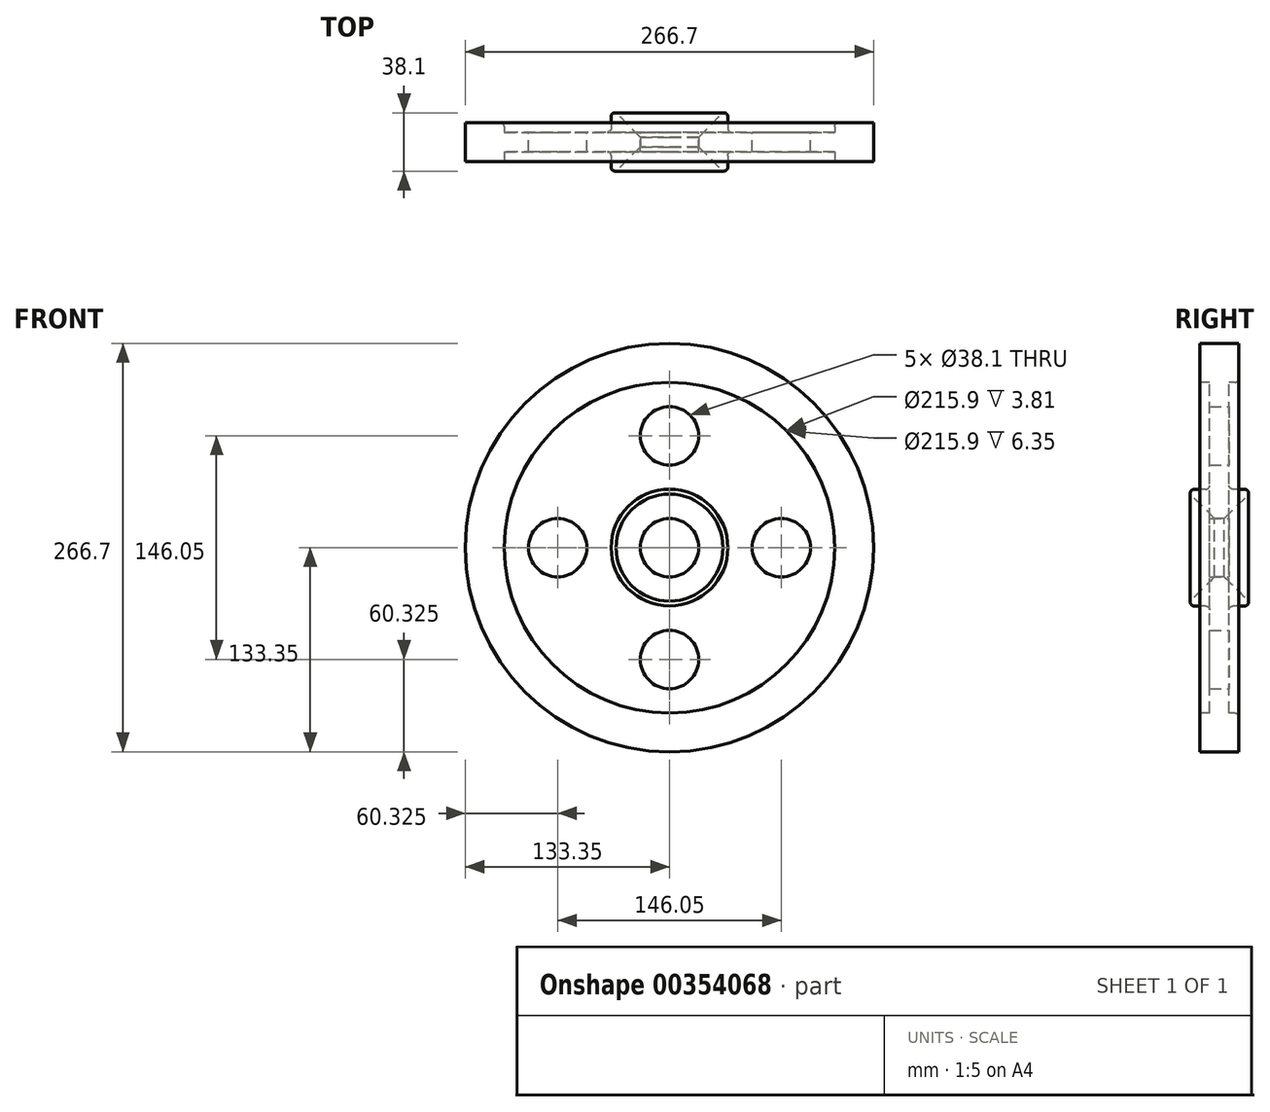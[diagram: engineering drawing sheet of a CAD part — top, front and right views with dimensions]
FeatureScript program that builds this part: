
annotation { "Feature Type Name" : "Feature", "Feature Type Description" : "" }
export const myFeature = defineFeature(function(context is Context, id is Id, definition is map)
    precondition{}
    {
        {
            var Q0;
            Q0=qCreatedBy(makeId("Right.planeOp"),FACE);
            var sketch = newSketch(context, id + "F0", { "sketchPlane" : qUnion([Q0])});
            skLineSegment(sketch, "E0", {"start": v(0, 0) * mm, "end": v(19.05, 0) * mm, "construction": true});
            skLineSegment(sketch, "E1.0", {"start": v(0, 19.05) * mm, "end": v(19.05, 19.05) * mm});
            skLineSegment(sketch, "E2.0", {"start": v(6.35, 38.1) * mm, "end": v(19.05, 38.1) * mm});
            skLineSegment(sketch, "E3.0", {"start": v(6.35, 107.95) * mm, "end": v(12.7, 107.95) * mm});
            skLineSegment(sketch, "E4.0", {"start": v(0, 133.35) * mm, "end": v(12.7, 133.35) * mm});
            skLineSegment(sketch, "E5", {"start": v(0, 0) * mm, "end": v(0, 133.35) * mm, "construction": true});
            skLineSegment(sketch, "E6.0", {"start": v(6.35, 38.1) * mm, "end": v(6.35, 107.95) * mm});
            skLineSegment(sketch, "E7.0", {"start": v(19.05, 19.05) * mm, "end": v(19.05, 38.1) * mm});
            skLineSegment(sketch, "E8.trimOffspring", {"start": v(12.7, 107.95) * mm, "end": v(12.7, 133.35) * mm});
            skLineSegment(sketch, "E9.MirrorCS", {"start": v(-6.35, 38.1) * mm, "end": v(-6.35, 107.95) * mm});
            skLineSegment(sketch, "E10.MirrorCS", {"start": v(-12.7, 107.95) * mm, "end": v(-12.7, 133.35) * mm});
            skLineSegment(sketch, "E11.MirrorCS", {"start": v(0, 133.35) * mm, "end": v(-12.7, 133.35) * mm});
            skLineSegment(sketch, "E12.MirrorCS", {"start": v(-6.35, 38.1) * mm, "end": v(-19.05, 38.1) * mm});
            skLineSegment(sketch, "E13.MirrorCS", {"start": v(-19.05, 19.05) * mm, "end": v(-19.05, 38.1) * mm});
            skLineSegment(sketch, "E14.MirrorCS", {"start": v(0, 19.05) * mm, "end": v(-19.05, 19.05) * mm});
            skLineSegment(sketch, "E15.MirrorCS", {"start": v(0, 0) * mm, "end": v(-19.05, 0) * mm, "construction": true});
            skLineSegment(sketch, "E16", {"start": v(-12.7, 107.95) * mm, "end": v(-6.35, 107.95) * mm});
            skPoint(sketch, "E17.orphan", {"position": v(0, 38.1) * mm});
            skSolve(sketch);
        }
        {
            var Q0;
            Q0=makeQuery(id+"F0.imprint","IMPRINT",FACE,{"disambiguationData":[TD([[makeQuery(id+"F0.imprint","IMPRINT",EDGE,{"derivedFrom":sQuery(id+"F0.wireOp",EDGE,"E1.0")}),1.0]])]});
            var Q1;
            Q1=sQuery(id+"F0.wireOp",EDGE,"E0");
            revolve(context, id + "F1", {"entities" : qUnion([Q0]), "axis" : qUnion([Q1]), "revolveType" : RevolveType.FULL});
        }
        {
            var Q0;
            Q0=makeQuery(id+"F1.opRevolve","SWEPT_FACE",FACE,{"disambiguationData":[OSD([sQuery(id+"F0.wireOp",EDGE,"E6.0")])]});
            var sketch = newSketch(context, id + "F2", { "sketchPlane" : qUnion([Q0])});
            skLineSegment(sketch, "E18", {"start": v(0, 0) * mm, "end": v(0, 73.03) * mm});
            skCircle(sketch, "E19", {"center": v(0, 73.03) * mm, "radius": 19.05 * mm});
            skCircle(sketch, "E20.1.0", {"center": v(-73.03, 0) * mm, "radius": 19.05 * mm});
            skCircle(sketch, "E20.2.0", {"center": v(0, -73.03) * mm, "radius": 19.05 * mm});
            skCircle(sketch, "E20.3.0", {"center": v(73.03, 0) * mm, "radius": 19.05 * mm});
            skPoint(sketch, "E20.center", {"position": v(0, 0) * mm});
            skSolve(sketch);
        }
        {
            var Q0;
            Q0=makeQuery(id+"F2.imprint","IMPRINT",FACE,{"disambiguationData":[TD([[makeQuery(id+"F2.imprint","IMPRINT",EDGE,{"derivedFrom":sQuery(id+"F2.wireOp",EDGE,"E20.1.0")}),1.0]])]});
            var Q1;
            Q1=makeQuery(id+"F2.imprint","IMPRINT",FACE,{"disambiguationData":[TD([[makeQuery(id+"F2.imprint","IMPRINT",EDGE,{"derivedFrom":sQuery(id+"F2.wireOp",EDGE,"E19")}),1.0]])]});
            var Q2;
            Q2=makeQuery(id+"F2.imprint","IMPRINT",FACE,{"disambiguationData":[TD([[makeQuery(id+"F2.imprint","IMPRINT",EDGE,{"derivedFrom":sQuery(id+"F2.wireOp",EDGE,"E20.3.0")}),1.0]])]});
            var Q3;
            Q3=makeQuery(id+"F2.imprint","IMPRINT",FACE,{"disambiguationData":[TD([[makeQuery(id+"F2.imprint","IMPRINT",EDGE,{"derivedFrom":sQuery(id+"F2.wireOp",EDGE,"E20.2.0")}),1.0]])]});
            extrude(context, id + "F3", {"entities" : qUnion([Q0, Q1, Q2, Q3]), "operationType" : NewBodyOperationType.REMOVE, "oppositeDirection" : true, "depth" : 25.4 * mm});
        }
        {
            var Q0;
            Q0=makeQuery(id+"F1.opRevolve","SWEPT_EDGE",EDGE,{"disambiguationData":[OSD([sQuery(id+"F0.wireOp",EDGE,"E2.0"),sQuery(id+"F0.wireOp",EDGE,"E6.0")])]});
            var Q1;
            Q1=makeQuery(id+"F1.opRevolve","SWEPT_EDGE",EDGE,{"disambiguationData":[OSD([sQuery(id+"F0.wireOp",EDGE,"E2.0"),sQuery(id+"F0.wireOp",EDGE,"E7.0")])]});
            var Q2;
            Q2=makeQuery(id+"F1.opRevolve","SWEPT_EDGE",EDGE,{"disambiguationData":[OSD([sQuery(id+"F0.wireOp",EDGE,"E3.0"),sQuery(id+"F0.wireOp",EDGE,"E8.trimOffspring")])]});
            fillet(context, id + "F4", {"entities" : qUnion([Q0, Q1, Q2]), "radius" : 2.54 * mm, "tangentPropagation" : true, "allowEdgeOverflow" : false});
        }
        {
            var Q0;
            Q0=makeQuery(id+"F1.opRevolve","SWEPT_EDGE",EDGE,{"disambiguationData":[OSD([sQuery(id+"F0.wireOp",EDGE,"E9.MirrorCS"),sQuery(id+"F0.wireOp",EDGE,"E12.MirrorCS")])]});
            var Q1;
            Q1=makeQuery(id+"F1.opRevolve","SWEPT_FACE",FACE,{"disambiguationData":[OSD([sQuery(id+"F0.wireOp",EDGE,"E12.MirrorCS")])]});
            fillet(context, id + "F5", {"entities" : qUnion([Q0, Q1]), "radius" : 2.54 * mm, "tangentPropagation" : true, "allowEdgeOverflow" : false});
        }
        {
            var Q0;
            Q0=makeQuery(id+"F1.opRevolve","SWEPT_EDGE",EDGE,{"disambiguationData":[OSD([sQuery(id+"F0.wireOp",EDGE,"E1.0"),sQuery(id+"F0.wireOp",EDGE,"E7.0")])]});
            var Q1;
            Q1=makeQuery(id+"F1.opRevolve","SWEPT_EDGE",EDGE,{"disambiguationData":[OSD([sQuery(id+"F0.wireOp",EDGE,"E13.MirrorCS"),sQuery(id+"F0.wireOp",EDGE,"E14.MirrorCS")])]});
            chamfer(context, id + "F6", {"entities" : qUnion([Q0, Q1]), "width" : 15.88 * mm, "tangentPropagation" : true});
        }
    });
